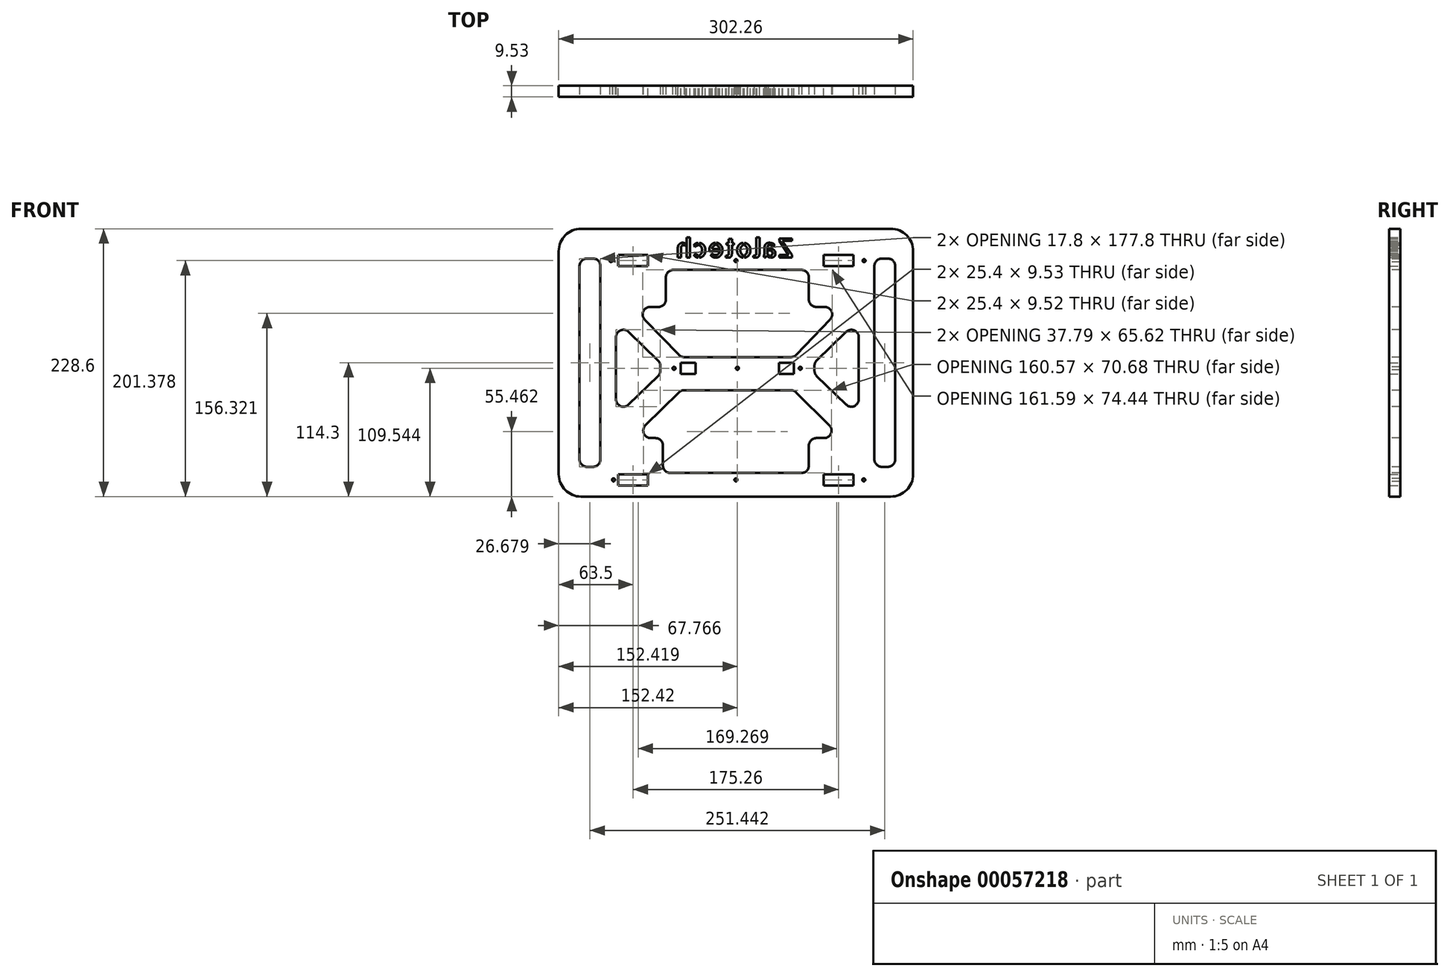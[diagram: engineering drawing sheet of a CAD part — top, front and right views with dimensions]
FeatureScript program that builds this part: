
annotation { "Feature Type Name" : "Feature", "Feature Type Description" : "" }
export const myFeature = defineFeature(function(context is Context, id is Id, definition is map)
    precondition{}
    {
        {
            var Q0;
            Q0=qCreatedBy(makeId("Front.planeOp"),FACE);
            var sketch = newSketch(context, id + "F0", { "sketchPlane" : qUnion([Q0])});
            skLineSegment(sketch, "E0.bottom", {"start": v(-133.35, 114.3) * mm, "end": v(130.8, 114.3) * mm});
            skLineSegment(sketch, "E0.top", {"start": v(-133.35, -114.3) * mm, "end": v(130.8, -114.3) * mm});
            skLineSegment(sketch, "E0.left", {"start": v(-152.4, 95.25) * mm, "end": v(-152.4, -95.25) * mm});
            skLineSegment(sketch, "E0.right", {"start": v(149.86, 95.25) * mm, "end": v(149.86, -95.25) * mm});
            skLineSegment(sketch, "E1", {"start": v(-152.4, -95.25) * mm, "end": v(-101.6, -95.25) * mm, "construction": true});
            skLineSegment(sketch, "E2", {"start": v(149.86, -95.25) * mm, "end": v(99.06, -95.25) * mm, "construction": true});
            skLineSegment(sketch, "E3", {"start": v(-101.6, -95.25) * mm, "end": v(-101.6, -114.3) * mm, "construction": true});
            skLineSegment(sketch, "E4", {"start": v(99.06, -95.25) * mm, "end": v(99.06, -114.3) * mm, "construction": true});
            skPoint(sketch, "E5.oppositeSnap0", {"position": v(-101.6, -104.78) * mm});
            skLineSegment(sketch, "E5.bottom", {"start": v(-101.6, -95.25) * mm, "end": v(-76.2, -95.25) * mm});
            skLineSegment(sketch, "E5.top", {"start": v(-101.6, -104.78) * mm, "end": v(-76.2, -104.78) * mm});
            skLineSegment(sketch, "E5.left", {"start": v(-101.6, -95.25) * mm, "end": v(-101.6, -104.78) * mm});
            skLineSegment(sketch, "E5.right", {"start": v(-76.2, -95.25) * mm, "end": v(-76.2, -104.78) * mm});
            skLineSegment(sketch, "E6.bottom", {"start": v(99.06, -95.25) * mm, "end": v(73.66, -95.25) * mm});
            skLineSegment(sketch, "E6.top", {"start": v(99.06, -104.78) * mm, "end": v(73.66, -104.78) * mm});
            skLineSegment(sketch, "E6.left", {"start": v(99.06, -95.25) * mm, "end": v(99.06, -104.78) * mm});
            skLineSegment(sketch, "E6.right", {"start": v(73.66, -95.25) * mm, "end": v(73.66, -104.78) * mm});
            skLineSegment(sketch, "E7", {"start": v(48.26, 0) * mm, "end": v(-48.26, 0) * mm, "construction": true});
            skLineSegment(sketch, "E8.bottom", {"start": v(48.26, 0) * mm, "end": v(35.56, 0) * mm});
            skLineSegment(sketch, "E8.top", {"start": v(48.26, -9.52) * mm, "end": v(35.56, -9.52) * mm});
            skLineSegment(sketch, "E8.left", {"start": v(48.26, 0) * mm, "end": v(48.26, -9.52) * mm});
            skLineSegment(sketch, "E8.right", {"start": v(35.56, 0) * mm, "end": v(35.56, -9.52) * mm});
            skLineSegment(sketch, "E9.bottom", {"start": v(-48.26, 0) * mm, "end": v(-35.56, 0) * mm});
            skLineSegment(sketch, "E9.top", {"start": v(-48.26, -9.53) * mm, "end": v(-35.56, -9.53) * mm});
            skLineSegment(sketch, "E9.left", {"start": v(-48.26, 0) * mm, "end": v(-48.26, -9.53) * mm});
            skLineSegment(sketch, "E9.right", {"start": v(-35.56, 0) * mm, "end": v(-35.56, -9.53) * mm});
            skLineSegment(sketch, "E10", {"start": v(-101.6, -95.25) * mm, "end": v(-101.6, 91.84) * mm, "construction": true});
            skLineSegment(sketch, "E11", {"start": v(-76.2, -95.25) * mm, "end": v(-76.2, 91.84) * mm, "construction": true});
            skLineSegment(sketch, "E12", {"start": v(-101.6, 91.84) * mm, "end": v(-76.2, 91.84) * mm, "construction": true});
            skLineSegment(sketch, "E13", {"start": v(-101.6, 91.84) * mm, "end": v(108.78, 91.84) * mm, "construction": true});
            skLineSegment(sketch, "E14", {"start": v(99.06, -95.25) * mm, "end": v(99.06, 91.84) * mm, "construction": true});
            skLineSegment(sketch, "E15", {"start": v(73.66, -95.25) * mm, "end": v(73.66, 91.84) * mm, "construction": true});
            skLineSegment(sketch, "E16.bottom", {"start": v(-101.6, 91.84) * mm, "end": v(-76.2, 91.84) * mm});
            skLineSegment(sketch, "E16.top", {"start": v(-101.6, 82.32) * mm, "end": v(-76.2, 82.32) * mm});
            skLineSegment(sketch, "E16.left", {"start": v(-101.6, 91.84) * mm, "end": v(-101.6, 82.32) * mm});
            skLineSegment(sketch, "E16.right", {"start": v(-76.2, 91.84) * mm, "end": v(-76.2, 82.32) * mm});
            skLineSegment(sketch, "E17.bottom", {"start": v(73.66, 91.84) * mm, "end": v(99.06, 91.84) * mm});
            skLineSegment(sketch, "E17.top", {"start": v(73.66, 82.32) * mm, "end": v(99.06, 82.32) * mm});
            skLineSegment(sketch, "E17.left", {"start": v(73.66, 91.84) * mm, "end": v(73.66, 82.32) * mm});
            skLineSegment(sketch, "E17.right", {"start": v(99.06, 91.84) * mm, "end": v(99.06, 82.32) * mm});
            skPoint(sketch, "E18.visualSharp", {"position": v(-152.4, 114.3) * mm});
            skArc(sketch, "E18.filletArc", {"start": v(-133.35, 114.3) * mm, "mid": v(-146.82, 108.72) * mm, "end": v(-152.4, 95.25) * mm});
            skPoint(sketch, "E19.visualSharp", {"position": v(149.86, 114.3) * mm});
            skArc(sketch, "E19.filletArc", {"start": v(149.86, 95.25) * mm, "mid": v(144.28, 108.72) * mm, "end": v(130.8, 114.3) * mm});
            skPoint(sketch, "E20.visualSharp", {"position": v(149.86, -114.3) * mm});
            skArc(sketch, "E20.filletArc", {"start": v(130.8, -114.3) * mm, "mid": v(144.28, -108.72) * mm, "end": v(149.86, -95.25) * mm});
            skPoint(sketch, "E21.visualSharp", {"position": v(-152.4, -114.3) * mm});
            skArc(sketch, "E21.filletArc", {"start": v(-152.4, -95.25) * mm, "mid": v(-146.82, -108.72) * mm, "end": v(-133.35, -114.3) * mm});
            skSolve(sketch);
        }
        {
            var Q0;
            Q0=makeQuery(id+"F0.imprint","IMPRINT",FACE,{"disambiguationData":[TD([[makeQuery(id+"F0.imprint","IMPRINT",EDGE,{"derivedFrom":sQuery(id+"F0.wireOp",EDGE,"E0.bottom")}),-1.0]])]});
            extrude(context, id + "F1", {"entities" : qUnion([Q0]), "depth" : 9.52 * mm});
        }
        {
            var Q0;
            Q0=makeQuery(id+"F1.opExtrude","CAP_FACE",FACE,{"disambiguationData":[OSD([sQuery(id+"F0.wireOp",EDGE,"E0.bottom"),sQuery(id+"F0.wireOp",EDGE,"E0.top"),sQuery(id+"F0.wireOp",EDGE,"E0.left"),sQuery(id+"F0.wireOp",EDGE,"E0.right"),sQuery(id+"F0.wireOp",EDGE,"E5.bottom"),sQuery(id+"F0.wireOp",EDGE,"E5.top"),sQuery(id+"F0.wireOp",EDGE,"E5.left"),sQuery(id+"F0.wireOp",EDGE,"E5.right"),sQuery(id+"F0.wireOp",EDGE,"E6.bottom"),sQuery(id+"F0.wireOp",EDGE,"E6.top"),sQuery(id+"F0.wireOp",EDGE,"E6.left"),sQuery(id+"F0.wireOp",EDGE,"E6.right"),sQuery(id+"F0.wireOp",EDGE,"E8.bottom"),sQuery(id+"F0.wireOp",EDGE,"E8.top"),sQuery(id+"F0.wireOp",EDGE,"E8.left"),sQuery(id+"F0.wireOp",EDGE,"E8.right"),sQuery(id+"F0.wireOp",EDGE,"E9.bottom"),sQuery(id+"F0.wireOp",EDGE,"E9.top"),sQuery(id+"F0.wireOp",EDGE,"E9.left"),sQuery(id+"F0.wireOp",EDGE,"E9.right"),sQuery(id+"F0.wireOp",EDGE,"E16.bottom"),sQuery(id+"F0.wireOp",EDGE,"E16.top"),sQuery(id+"F0.wireOp",EDGE,"E16.left"),sQuery(id+"F0.wireOp",EDGE,"E16.right"),sQuery(id+"F0.wireOp",EDGE,"E17.bottom"),sQuery(id+"F0.wireOp",EDGE,"E17.top"),sQuery(id+"F0.wireOp",EDGE,"E17.left"),sQuery(id+"F0.wireOp",EDGE,"E17.right")])],"isStart":false});
            var sketch = newSketch(context, id + "F2", { "sketchPlane" : qUnion([Q0])});
            skLineSegment(sketch, "E22", {"start": v(-63.5, -77.67) * mm, "end": v(-63.5, -87.83) * mm});
            skLineSegment(sketch, "E23", {"start": v(-57.15, -94.18) * mm, "end": v(54.6, -94.18) * mm});
            skLineSegment(sketch, "E24", {"start": v(60.96, -87.83) * mm, "end": v(60.96, -77.67) * mm});
            skLineSegment(sketch, "E25", {"start": v(-54.6, 79.24) * mm, "end": v(54.6, 79.24) * mm});
            skLineSegment(sketch, "E26", {"start": v(-45.5, 4.8) * mm, "end": v(45.66, 4.8) * mm});
            skLineSegment(sketch, "E27", {"start": v(74.5, 47.62) * mm, "end": v(67.18, 47.62) * mm});
            skLineSegment(sketch, "E28.MirrorCS", {"start": v(-74.47, 47.62) * mm, "end": v(-67.18, 47.62) * mm});
            skLineSegment(sketch, "E29", {"start": v(-50.09, 6.75) * mm, "end": v(-79.04, 36.87) * mm});
            skLineSegment(sketch, "E30", {"start": v(50.24, 6.76) * mm, "end": v(79.1, 36.88) * mm});
            skLineSegment(sketch, "E31", {"start": v(-60.96, 53.84) * mm, "end": v(-60.96, 72.9) * mm});
            skLineSegment(sketch, "E32", {"start": v(60.96, 53.84) * mm, "end": v(60.96, 72.9) * mm});
            skLineSegment(sketch, "E33", {"start": v(-45.5, -23.5) * mm, "end": v(45.66, -23.5) * mm});
            skLineSegment(sketch, "E34", {"start": v(89.38, 47.62) * mm, "end": v(89.38, -82.33) * mm, "construction": true});
            skLineSegment(sketch, "E35", {"start": v(60.96, 47.62) * mm, "end": v(-60.96, 47.62) * mm, "construction": true});
            skLineSegment(sketch, "E36", {"start": v(-78.41, -53.5) * mm, "end": v(-49.98, -25.33) * mm});
            skLineSegment(sketch, "E37", {"start": v(50.14, -25.34) * mm, "end": v(78.46, -53.51) * mm});
            skLineSegment(sketch, "E38", {"start": v(-63.5, -77.67) * mm, "end": v(-63.5, -70.71) * mm});
            skLineSegment(sketch, "E39", {"start": v(60.96, -77.67) * mm, "end": v(60.96, -70.71) * mm});
            skLineSegment(sketch, "E40", {"start": v(73.99, -64.36) * mm, "end": v(67.3, -64.36) * mm});
            skLineSegment(sketch, "E41", {"start": v(-69.85, -64.36) * mm, "end": v(-73.95, -64.36) * mm});
            skArc(sketch, "E42.filletArc", {"start": v(-74.47, 47.62) * mm, "mid": v(-80.3, 43.76) * mm, "end": v(-79.04, 36.87) * mm});
            skPoint(sketch, "E43.visualSharp", {"position": v(89.38, 47.62) * mm});
            skArc(sketch, "E43.filletArc", {"start": v(79.1, 36.88) * mm, "mid": v(80.34, 43.76) * mm, "end": v(74.5, 47.62) * mm});
            skPoint(sketch, "E44.visualSharp", {"position": v(48.37, 4.8) * mm});
            skArc(sketch, "E44.filletArc", {"start": v(45.66, 4.8) * mm, "mid": v(48.15, 5.3) * mm, "end": v(50.24, 6.76) * mm});
            skPoint(sketch, "E45.visualSharp", {"position": v(-48.21, 4.8) * mm});
            skArc(sketch, "E45.filletArc", {"start": v(-50.09, 6.75) * mm, "mid": v(-48, 5.3) * mm, "end": v(-45.5, 4.8) * mm});
            skPoint(sketch, "E46.visualSharp", {"position": v(-48.12, -23.5) * mm});
            skArc(sketch, "E46.filletArc", {"start": v(-45.5, -23.5) * mm, "mid": v(-47.92, -23.97) * mm, "end": v(-49.98, -25.33) * mm});
            skPoint(sketch, "E47.visualSharp", {"position": v(48.28, -23.5) * mm});
            skArc(sketch, "E47.filletArc", {"start": v(50.14, -25.34) * mm, "mid": v(48.08, -23.97) * mm, "end": v(45.66, -23.5) * mm});
            skPoint(sketch, "E48.visualSharp", {"position": v(89.38, -64.36) * mm});
            skArc(sketch, "E48.filletArc", {"start": v(73.99, -64.36) * mm, "mid": v(79.86, -60.44) * mm, "end": v(78.46, -53.51) * mm});
            skArc(sketch, "E49.filletArc", {"start": v(-78.41, -53.5) * mm, "mid": v(-79.82, -60.43) * mm, "end": v(-73.95, -64.36) * mm});
            skPoint(sketch, "E50.visualSharp", {"position": v(-63.5, -64.36) * mm});
            skArc(sketch, "E50.filletArc", {"start": v(-63.5, -70.71) * mm, "mid": v(-65.36, -66.22) * mm, "end": v(-69.85, -64.36) * mm});
            skPoint(sketch, "E51.visualSharp", {"position": v(60.96, -64.36) * mm});
            skArc(sketch, "E51.filletArc", {"start": v(67.3, -64.36) * mm, "mid": v(62.82, -66.22) * mm, "end": v(60.96, -70.71) * mm});
            skArc(sketch, "E52.filletArc", {"start": v(-67.18, 47.62) * mm, "mid": v(-62.78, 49.44) * mm, "end": v(-60.96, 53.84) * mm});
            skArc(sketch, "E53.filletArc", {"start": v(60.96, 53.84) * mm, "mid": v(62.78, 49.44) * mm, "end": v(67.18, 47.62) * mm});
            skArc(sketch, "E54.filletArc", {"start": v(-54.6, 79.24) * mm, "mid": v(-59.1, 77.38) * mm, "end": v(-60.96, 72.9) * mm});
            skArc(sketch, "E55.filletArc", {"start": v(60.96, 72.9) * mm, "mid": v(59.1, 77.38) * mm, "end": v(54.6, 79.24) * mm});
            skPoint(sketch, "E56.visualSharp", {"position": v(-63.5, -94.18) * mm});
            skArc(sketch, "E56.filletArc", {"start": v(-63.5, -87.83) * mm, "mid": v(-61.64, -92.32) * mm, "end": v(-57.15, -94.18) * mm});
            skPoint(sketch, "E57.visualSharp", {"position": v(60.96, -94.18) * mm});
            skArc(sketch, "E57.filletArc", {"start": v(54.6, -94.18) * mm, "mid": v(59.1, -92.32) * mm, "end": v(60.96, -87.83) * mm});
            skSolve(sketch);
        }
        {
            var Q0;
            Q0=makeQuery(id+"F2.imprint","IMPRINT",FACE,{"disambiguationData":[TD([[makeQuery(id+"F2.imprint","IMPRINT",EDGE,{"derivedFrom":sQuery(id+"F2.wireOp",EDGE,"E26")}),1.0]])]});
            var Q1;
            {var subQ3=sQuery(id+"F2.wireOp",EDGE,"E23");Q1=makeQuery(id+"F2.imprint","IMPRINT",FACE,{"disambiguationData":[TD([[makeQuery(id+"F2.imprint","IMPRINT",EDGE,{"derivedFrom":subQ3}),1.0]])]});}
            var Q2;
            Q2=makeQuery(id+"F2.imprint","IMPRINT",FACE,{"disambiguationData":[TD([[makeQuery(id+"F2.imprint","IMPRINT",EDGE,{"derivedFrom":sQuery(id+"F2.wireOp",EDGE,"f44173c2-0543-4982-a62a-dc314a2ca8c5")}),-1.0]])]});
            var Q3;
            Q3=makeQuery(id+"F2.imprint","IMPRINT",FACE,{"disambiguationData":[TD([[makeQuery(id+"F2.imprint","IMPRINT",EDGE,{"derivedFrom":sQuery(id+"F2.wireOp",EDGE,"1ee7fdb6-237e-4fa8-abf3-a4b38ba9088a0.MirrorCS")}),1.0]])]});
            extrude(context, id + "F3", {"entities" : qUnion([Q0, Q1, Q2, Q3]), "operationType" : NewBodyOperationType.REMOVE, "oppositeDirection" : true, "depth" : 25.4 * mm});
        }
        {
            var Q0;
            Q0=makeQuery(id+"F1.opExtrude","CAP_FACE",FACE,{"disambiguationData":[OSD([sQuery(id+"F0.wireOp",EDGE,"E0.bottom"),sQuery(id+"F0.wireOp",EDGE,"E0.top"),sQuery(id+"F0.wireOp",EDGE,"E0.left"),sQuery(id+"F0.wireOp",EDGE,"E0.right"),sQuery(id+"F0.wireOp",EDGE,"E5.bottom"),sQuery(id+"F0.wireOp",EDGE,"E5.top"),sQuery(id+"F0.wireOp",EDGE,"E5.left"),sQuery(id+"F0.wireOp",EDGE,"E5.right"),sQuery(id+"F0.wireOp",EDGE,"E6.bottom"),sQuery(id+"F0.wireOp",EDGE,"E6.top"),sQuery(id+"F0.wireOp",EDGE,"E6.left"),sQuery(id+"F0.wireOp",EDGE,"E6.right"),sQuery(id+"F0.wireOp",EDGE,"E8.bottom"),sQuery(id+"F0.wireOp",EDGE,"E8.top"),sQuery(id+"F0.wireOp",EDGE,"E8.left"),sQuery(id+"F0.wireOp",EDGE,"E8.right"),sQuery(id+"F0.wireOp",EDGE,"E9.bottom"),sQuery(id+"F0.wireOp",EDGE,"E9.top"),sQuery(id+"F0.wireOp",EDGE,"E9.left"),sQuery(id+"F0.wireOp",EDGE,"E9.right"),sQuery(id+"F0.wireOp",EDGE,"E16.bottom"),sQuery(id+"F0.wireOp",EDGE,"E16.top"),sQuery(id+"F0.wireOp",EDGE,"E16.left"),sQuery(id+"F0.wireOp",EDGE,"E16.right"),sQuery(id+"F0.wireOp",EDGE,"E17.bottom"),sQuery(id+"F0.wireOp",EDGE,"E17.top"),sQuery(id+"F0.wireOp",EDGE,"E17.left"),sQuery(id+"F0.wireOp",EDGE,"E17.right"),sQuery(id+"F0.wireOp",EDGE,"E18.filletArc"),sQuery(id+"F0.wireOp",EDGE,"E19.filletArc"),sQuery(id+"F0.wireOp",EDGE,"E20.filletArc"),sQuery(id+"F0.wireOp",EDGE,"E21.filletArc")])],"isStart":false});
            var sketch = newSketch(context, id + "F4", { "sketchPlane" : qUnion([Q0])});
            skLineSegment(sketch, "E58", {"start": v(134.62, 82.55) * mm, "end": v(134.62, -82.55) * mm});
            skLineSegment(sketch, "E59.MirrorCS", {"start": v(-134.62, 88.9) * mm, "end": v(-134.62, -88.9) * mm});
            skLineSegment(sketch, "E60.bottom", {"start": v(-128.27, -88.9) * mm, "end": v(-123.17, -88.9) * mm});
            skLineSegment(sketch, "E60.top", {"start": v(-128.27, 88.9) * mm, "end": v(-123.17, 88.9) * mm});
            skLineSegment(sketch, "E60.left", {"start": v(-134.62, -82.55) * mm, "end": v(-134.62, 82.55) * mm});
            skLineSegment(sketch, "E60.right", {"start": v(-116.82, -82.55) * mm, "end": v(-116.82, 82.55) * mm});
            skLineSegment(sketch, "E61.MirrorCS", {"start": v(116.82, -82.55) * mm, "end": v(116.82, 82.55) * mm});
            skLineSegment(sketch, "E62.MirrorCS", {"start": v(128.27, 88.9) * mm, "end": v(123.17, 88.9) * mm});
            skLineSegment(sketch, "E63.MirrorCS", {"start": v(128.27, -88.9) * mm, "end": v(123.17, -88.9) * mm});
            skPoint(sketch, "E64.visualSharp", {"position": v(-116.82, 88.9) * mm});
            skArc(sketch, "E64.filletArc", {"start": v(-116.82, 82.55) * mm, "mid": v(-118.68, 87.04) * mm, "end": v(-123.17, 88.9) * mm});
            skPoint(sketch, "E65.visualSharp", {"position": v(-134.62, 88.9) * mm});
            skArc(sketch, "E65.filletArc", {"start": v(-128.27, 88.9) * mm, "mid": v(-132.76, 87.04) * mm, "end": v(-134.62, 82.55) * mm});
            skPoint(sketch, "E66.visualSharp", {"position": v(-116.82, -88.9) * mm});
            skArc(sketch, "E66.filletArc", {"start": v(-123.17, -88.9) * mm, "mid": v(-118.68, -87.04) * mm, "end": v(-116.82, -82.55) * mm});
            skPoint(sketch, "E67.visualSharp", {"position": v(-134.62, -88.9) * mm});
            skArc(sketch, "E67.filletArc", {"start": v(-134.62, -82.55) * mm, "mid": v(-132.76, -87.04) * mm, "end": v(-128.27, -88.9) * mm});
            skPoint(sketch, "E68.visualSharp", {"position": v(116.82, -88.9) * mm});
            skArc(sketch, "E68.filletArc", {"start": v(116.82, -82.55) * mm, "mid": v(118.68, -87.04) * mm, "end": v(123.17, -88.9) * mm});
            skPoint(sketch, "E69.visualSharp", {"position": v(134.62, -88.9) * mm});
            skArc(sketch, "E69.filletArc", {"start": v(128.27, -88.9) * mm, "mid": v(132.76, -87.04) * mm, "end": v(134.62, -82.55) * mm});
            skPoint(sketch, "E70.visualSharp", {"position": v(134.62, 88.9) * mm});
            skArc(sketch, "E70.filletArc", {"start": v(134.62, 82.55) * mm, "mid": v(132.76, 87.04) * mm, "end": v(128.27, 88.9) * mm});
            skPoint(sketch, "E71.visualSharp", {"position": v(116.82, 88.9) * mm});
            skArc(sketch, "E71.filletArc", {"start": v(123.17, 88.9) * mm, "mid": v(118.68, 87.04) * mm, "end": v(116.82, 82.55) * mm});
            skSolve(sketch);
        }
        {
            var Q0;
            Q0=qSketchRegion(id+"F4",true);
            extrude(context, id + "F5", {"entities" : qUnion([Q0]), "operationType" : NewBodyOperationType.REMOVE, "oppositeDirection" : true, "depth" : 25.4 * mm});
        }
        {
            var Q0;
            {var subQ3=sQuery(id+"F4.wireOp",EDGE,"E62.MirrorCS");Q0=makeQuery(id+"F4.imprint","IMPRINT",FACE,{"disambiguationData":[TD([[makeQuery(id+"F4.imprint","IMPRINT",EDGE,{"derivedFrom":subQ3}),1.0]])]});}
            var Q1;
            {var subQ3=sQuery(id+"F4.wireOp",EDGE,"E63.MirrorCS");Q1=makeQuery(id+"F4.imprint","IMPRINT",FACE,{"disambiguationData":[TD([[makeQuery(id+"F4.imprint","IMPRINT",EDGE,{"derivedFrom":subQ3}),-1.0]])]});}
            var Q2;
            {var subQ0=sQuery(id+"F4.wireOp",EDGE,"E60.bottom");Q2=makeQuery(id+"F4.imprint","IMPRINT",FACE,{"disambiguationData":[TD([[makeQuery(id+"F4.imprint","IMPRINT",EDGE,{"derivedFrom":subQ0}),1.0]])]});}
            var Q3;
            {var subQ5=sQuery(id+"F4.wireOp",EDGE,"E60.top");Q3=makeQuery(id+"F4.imprint","IMPRINT",FACE,{"disambiguationData":[TD([[makeQuery(id+"F4.imprint","IMPRINT",EDGE,{"derivedFrom":subQ5}),-1.0]])]});}
            extrude(context, id + "F6", {"entities" : qUnion([Q0, Q1, Q2, Q3]), "operationType" : NewBodyOperationType.REMOVE, "oppositeDirection" : true, "depth" : 25.4 * mm});
        }
        {
            var Q0;
            Q0=makeQuery(id+"F1.opExtrude","CAP_FACE",FACE,{"disambiguationData":[OSD([sQuery(id+"F0.wireOp",EDGE,"E0.bottom"),sQuery(id+"F0.wireOp",EDGE,"E0.top"),sQuery(id+"F0.wireOp",EDGE,"E0.left"),sQuery(id+"F0.wireOp",EDGE,"E0.right"),sQuery(id+"F0.wireOp",EDGE,"E5.bottom"),sQuery(id+"F0.wireOp",EDGE,"E5.top"),sQuery(id+"F0.wireOp",EDGE,"E5.left"),sQuery(id+"F0.wireOp",EDGE,"E5.right"),sQuery(id+"F0.wireOp",EDGE,"E6.bottom"),sQuery(id+"F0.wireOp",EDGE,"E6.top"),sQuery(id+"F0.wireOp",EDGE,"E6.left"),sQuery(id+"F0.wireOp",EDGE,"E6.right"),sQuery(id+"F0.wireOp",EDGE,"E8.bottom"),sQuery(id+"F0.wireOp",EDGE,"E8.top"),sQuery(id+"F0.wireOp",EDGE,"E8.left"),sQuery(id+"F0.wireOp",EDGE,"E8.right"),sQuery(id+"F0.wireOp",EDGE,"E9.bottom"),sQuery(id+"F0.wireOp",EDGE,"E9.top"),sQuery(id+"F0.wireOp",EDGE,"E9.left"),sQuery(id+"F0.wireOp",EDGE,"E9.right"),sQuery(id+"F0.wireOp",EDGE,"E16.bottom"),sQuery(id+"F0.wireOp",EDGE,"E16.top"),sQuery(id+"F0.wireOp",EDGE,"E16.left"),sQuery(id+"F0.wireOp",EDGE,"E16.right"),sQuery(id+"F0.wireOp",EDGE,"E17.bottom"),sQuery(id+"F0.wireOp",EDGE,"E17.top"),sQuery(id+"F0.wireOp",EDGE,"E17.left"),sQuery(id+"F0.wireOp",EDGE,"E17.right"),sQuery(id+"F0.wireOp",EDGE,"E18.filletArc"),sQuery(id+"F0.wireOp",EDGE,"E19.filletArc"),sQuery(id+"F0.wireOp",EDGE,"E20.filletArc"),sQuery(id+"F0.wireOp",EDGE,"E21.filletArc")])],"isStart":false});
            var sketch = newSketch(context, id + "F7", { "sketchPlane" : qUnion([Q0])});
            skCircle(sketch, "E72", {"center": v(-54.02, -4.76) * mm, "radius": 1.27 * mm});
            skCircle(sketch, "E73", {"center": v(0, -4.76) * mm, "radius": 1.27 * mm});
            skCircle(sketch, "E74", {"center": v(53.63, -4.76) * mm, "radius": 1.27 * mm});
            skLineSegment(sketch, "E75", {"start": v(-48.26, -4.76) * mm, "end": v(35.56, -4.76) * mm, "construction": true});
            skLineSegment(sketch, "E76", {"start": v(-101.6, 87.08) * mm, "end": v(99.06, 87.08) * mm, "construction": true});
            skCircle(sketch, "E77", {"center": v(-1.27, 87.08) * mm, "radius": 1.27 * mm});
            skCircle(sketch, "E78", {"center": v(-107.77, 87.08) * mm, "radius": 1.27 * mm});
            skCircle(sketch, "E79", {"center": v(108.04, 87.08) * mm, "radius": 1.27 * mm});
            skLineSegment(sketch, "E80", {"start": v(-101.6, -100.01) * mm, "end": v(99.06, -100.01) * mm, "construction": true});
            skCircle(sketch, "E81", {"center": v(-105.65, -100.01) * mm, "radius": 1.27 * mm});
            skCircle(sketch, "E82", {"center": v(-1.27, -100.01) * mm, "radius": 1.27 * mm});
            skCircle(sketch, "E83", {"center": v(107.77, -100.01) * mm, "radius": 1.27 * mm});
            skSolve(sketch);
        }
        {
            var Q0;
            Q0=qSketchRegion(id+"F7",true);
            extrude(context, id + "F8", {"entities" : qUnion([Q0]), "operationType" : NewBodyOperationType.REMOVE, "oppositeDirection" : true, "depth" : 25.4 * mm});
        }
        {
            var Q0;
            Q0=makeQuery(id+"F1.opExtrude","CAP_FACE",FACE,{"disambiguationData":[OSD([sQuery(id+"F0.wireOp",EDGE,"E0.bottom"),sQuery(id+"F0.wireOp",EDGE,"E0.top"),sQuery(id+"F0.wireOp",EDGE,"E0.left"),sQuery(id+"F0.wireOp",EDGE,"E0.right"),sQuery(id+"F0.wireOp",EDGE,"E5.bottom"),sQuery(id+"F0.wireOp",EDGE,"E5.top"),sQuery(id+"F0.wireOp",EDGE,"E5.left"),sQuery(id+"F0.wireOp",EDGE,"E5.right"),sQuery(id+"F0.wireOp",EDGE,"E6.bottom"),sQuery(id+"F0.wireOp",EDGE,"E6.top"),sQuery(id+"F0.wireOp",EDGE,"E6.left"),sQuery(id+"F0.wireOp",EDGE,"E6.right"),sQuery(id+"F0.wireOp",EDGE,"E8.bottom"),sQuery(id+"F0.wireOp",EDGE,"E8.top"),sQuery(id+"F0.wireOp",EDGE,"E8.left"),sQuery(id+"F0.wireOp",EDGE,"E8.right"),sQuery(id+"F0.wireOp",EDGE,"E9.bottom"),sQuery(id+"F0.wireOp",EDGE,"E9.top"),sQuery(id+"F0.wireOp",EDGE,"E9.left"),sQuery(id+"F0.wireOp",EDGE,"E9.right"),sQuery(id+"F0.wireOp",EDGE,"E16.bottom"),sQuery(id+"F0.wireOp",EDGE,"E16.top"),sQuery(id+"F0.wireOp",EDGE,"E16.left"),sQuery(id+"F0.wireOp",EDGE,"E16.right"),sQuery(id+"F0.wireOp",EDGE,"E17.bottom"),sQuery(id+"F0.wireOp",EDGE,"E17.top"),sQuery(id+"F0.wireOp",EDGE,"E17.left"),sQuery(id+"F0.wireOp",EDGE,"E17.right"),sQuery(id+"F0.wireOp",EDGE,"E18.filletArc"),sQuery(id+"F0.wireOp",EDGE,"E19.filletArc"),sQuery(id+"F0.wireOp",EDGE,"E20.filletArc"),sQuery(id+"F0.wireOp",EDGE,"E21.filletArc")])],"isStart":false});
            var sketch = newSketch(context, id + "F9", { "sketchPlane" : qUnion([Q0])});
            skLineSegment(sketch, "E84", {"start": v(-65.74, -4.76) * mm, "end": v(-65.74, -2.68) * mm});
            skPoint(sketch, "E84.startSnap0", {"position": v(-48.26, -4.76) * mm});
            skLineSegment(sketch, "E85", {"start": v(-65.74, -4.76) * mm, "end": v(-65.74, -6.83) * mm});
            skLineSegment(sketch, "E86", {"start": v(-67.66, -11.38) * mm, "end": v(-92.75, -35.8) * mm});
            skLineSegment(sketch, "E87", {"start": v(-103.53, -31.25) * mm, "end": v(-103.53, 21.74) * mm});
            skLineSegment(sketch, "E88", {"start": v(-67.66, 1.87) * mm, "end": v(-92.75, 26.29) * mm});
            skLineSegment(sketch, "E89.MirrorCS", {"start": v(65.74, -4.76) * mm, "end": v(65.74, -2.68) * mm});
            skLineSegment(sketch, "E90.MirrorCS", {"start": v(65.74, -4.76) * mm, "end": v(65.74, -6.83) * mm});
            skLineSegment(sketch, "E91.MirrorCS", {"start": v(67.66, 1.87) * mm, "end": v(92.75, 26.29) * mm});
            skLineSegment(sketch, "E92.MirrorCS", {"start": v(103.53, -31.25) * mm, "end": v(103.53, 21.74) * mm});
            skLineSegment(sketch, "E93.MirrorCS", {"start": v(67.66, -11.38) * mm, "end": v(92.75, -35.8) * mm});
            skPoint(sketch, "E94.visualSharp", {"position": v(-103.53, 36.78) * mm});
            skArc(sketch, "E94.filletArc", {"start": v(-92.75, 26.29) * mm, "mid": v(-99.65, 27.59) * mm, "end": v(-103.53, 21.74) * mm});
            skPoint(sketch, "E95.visualSharp", {"position": v(-103.53, -46.3) * mm});
            skArc(sketch, "E95.filletArc", {"start": v(-103.53, -31.25) * mm, "mid": v(-99.65, -37.1) * mm, "end": v(-92.75, -35.8) * mm});
            skPoint(sketch, "E96.visualSharp", {"position": v(-65.74, -9.51) * mm});
            skArc(sketch, "E96.filletArc", {"start": v(-67.66, -11.38) * mm, "mid": v(-66.24, -9.3) * mm, "end": v(-65.74, -6.83) * mm});
            skPoint(sketch, "E97.visualSharp", {"position": v(-65.74, 0) * mm});
            skArc(sketch, "E97.filletArc", {"start": v(-65.74, -2.68) * mm, "mid": v(-66.24, -0.21) * mm, "end": v(-67.66, 1.87) * mm});
            skPoint(sketch, "E98.visualSharp", {"position": v(65.74, -9.51) * mm});
            skArc(sketch, "E98.filletArc", {"start": v(65.74, -6.83) * mm, "mid": v(66.24, -9.3) * mm, "end": v(67.66, -11.38) * mm});
            skPoint(sketch, "E99.visualSharp", {"position": v(65.74, 0) * mm});
            skArc(sketch, "E99.filletArc", {"start": v(67.66, 1.87) * mm, "mid": v(66.24, -0.21) * mm, "end": v(65.74, -2.68) * mm});
            skPoint(sketch, "E100.visualSharp", {"position": v(103.53, 36.78) * mm});
            skArc(sketch, "E100.filletArc", {"start": v(103.53, 21.74) * mm, "mid": v(99.65, 27.59) * mm, "end": v(92.75, 26.29) * mm});
            skPoint(sketch, "E101.visualSharp", {"position": v(103.53, -46.3) * mm});
            skArc(sketch, "E101.filletArc", {"start": v(92.75, -35.8) * mm, "mid": v(99.65, -37.1) * mm, "end": v(103.53, -31.25) * mm});
            skSolve(sketch);
        }
        {
            var Q0;
            Q0=makeQuery(id+"F9.imprint","IMPRINT",FACE,{"disambiguationData":[TD([[makeQuery(id+"F9.imprint","IMPRINT",EDGE,{"derivedFrom":sQuery(id+"F9.wireOp",EDGE,"E84")}),1.0]])]});
            var Q1;
            Q1=makeQuery(id+"F9.imprint","IMPRINT",FACE,{"disambiguationData":[TD([[makeQuery(id+"F9.imprint","IMPRINT",EDGE,{"derivedFrom":sQuery(id+"F9.wireOp",EDGE,"E89.MirrorCS")}),-1.0]])]});
            extrude(context, id + "F10", {"entities" : qUnion([Q0, Q1]), "operationType" : NewBodyOperationType.REMOVE, "oppositeDirection" : true, "depth" : 25.4 * mm});
        }
        {
            var Q0;
            Q0=makeQuery(id+"F1.opExtrude","CAP_FACE",FACE,{"disambiguationData":[OSD([sQuery(id+"F0.wireOp",EDGE,"E0.bottom"),sQuery(id+"F0.wireOp",EDGE,"E0.top"),sQuery(id+"F0.wireOp",EDGE,"E0.left"),sQuery(id+"F0.wireOp",EDGE,"E0.right"),sQuery(id+"F0.wireOp",EDGE,"E5.bottom"),sQuery(id+"F0.wireOp",EDGE,"E5.top"),sQuery(id+"F0.wireOp",EDGE,"E5.left"),sQuery(id+"F0.wireOp",EDGE,"E5.right"),sQuery(id+"F0.wireOp",EDGE,"E6.bottom"),sQuery(id+"F0.wireOp",EDGE,"E6.top"),sQuery(id+"F0.wireOp",EDGE,"E6.left"),sQuery(id+"F0.wireOp",EDGE,"E6.right"),sQuery(id+"F0.wireOp",EDGE,"E8.bottom"),sQuery(id+"F0.wireOp",EDGE,"E8.top"),sQuery(id+"F0.wireOp",EDGE,"E8.left"),sQuery(id+"F0.wireOp",EDGE,"E8.right"),sQuery(id+"F0.wireOp",EDGE,"E9.bottom"),sQuery(id+"F0.wireOp",EDGE,"E9.top"),sQuery(id+"F0.wireOp",EDGE,"E9.left"),sQuery(id+"F0.wireOp",EDGE,"E9.right"),sQuery(id+"F0.wireOp",EDGE,"E16.bottom"),sQuery(id+"F0.wireOp",EDGE,"E16.top"),sQuery(id+"F0.wireOp",EDGE,"E16.left"),sQuery(id+"F0.wireOp",EDGE,"E16.right"),sQuery(id+"F0.wireOp",EDGE,"E17.bottom"),sQuery(id+"F0.wireOp",EDGE,"E17.top"),sQuery(id+"F0.wireOp",EDGE,"E17.left"),sQuery(id+"F0.wireOp",EDGE,"E17.right"),sQuery(id+"F0.wireOp",EDGE,"E18.filletArc"),sQuery(id+"F0.wireOp",EDGE,"E19.filletArc"),sQuery(id+"F0.wireOp",EDGE,"E20.filletArc"),sQuery(id+"F0.wireOp",EDGE,"E21.filletArc")])],"isStart":true});
            var sketch = newSketch(context, id + "F11", { "sketchPlane" : qUnion([Q0])});
            skText(sketch, "E102", { "text": "Zalotech", "fontName": "AllertaStencil-Regular.ttf"});
            skText(sketch, "E103", { "text": "Zalotech", "fontName": "AllertaStencil-Regular.ttf"});
            const initialGuessF11  = {"E102": [-0.04819, 0.0898, 1, 0, 0.01626], "E103": [-0.25287, 0.21927, 1, 0, 0.01833]};
            skSetInitialGuess(sketch, initialGuessF11);
            skSolve(sketch);
        }
        {
            var Q0;
            Q0=qSketchRegion(id+"F11",true);
            extrude(context, id + "F12", {"entities" : qUnion([Q0]), "operationType" : NewBodyOperationType.REMOVE, "oppositeDirection" : true, "depth" : 25.4 * mm});
        }
    });
